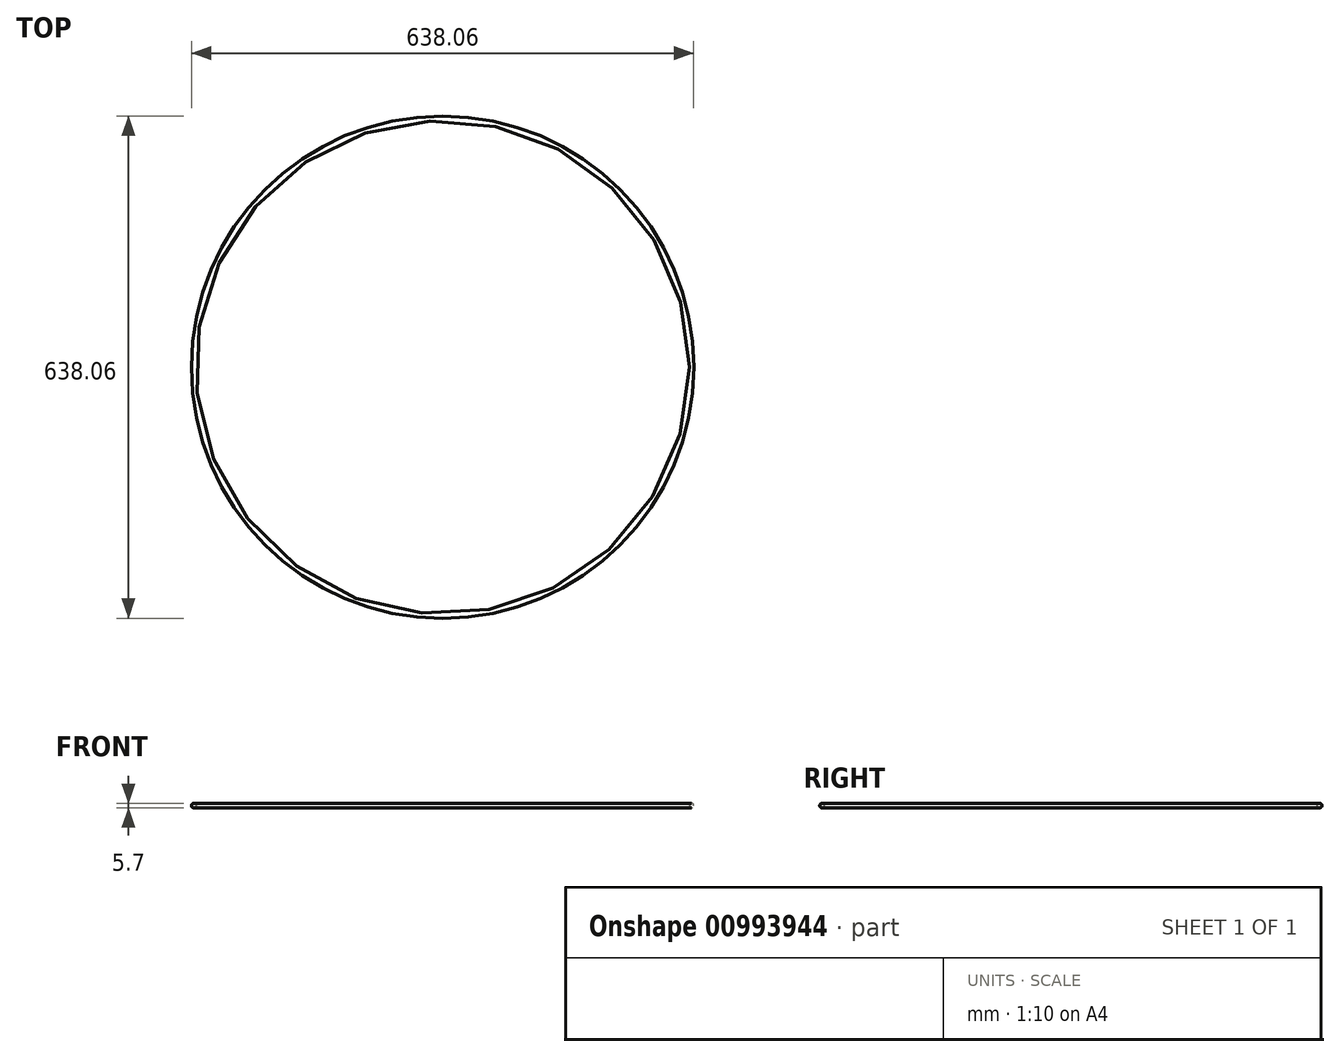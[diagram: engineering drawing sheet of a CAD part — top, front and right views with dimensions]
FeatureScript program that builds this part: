
annotation { "Feature Type Name" : "Feature", "Feature Type Description" : "" }
export const myFeature = defineFeature(function(context is Context, id is Id, definition is map)
    precondition{}
    {
        {
            var Q0;
            Q0=qCreatedBy(makeId("Top.planeOp"),FACE);
            var sketch = newSketch(context, id + "F0", { "sketchPlane" : qUnion([Q0])});
            skCircle(sketch, "E0", {"center": v(0, 0) * mm, "radius": 316.25 * mm});
            skSolve(sketch);
        }
        {
            var Q0;
            Q0=qCreatedBy(makeId("Front.planeOp"),FACE);
            var sketch = newSketch(context, id + "F1", { "sketchPlane" : qUnion([Q0])});
            skCircle(sketch, "E1", {"center": v(-316.18, 0) * mm, "radius": 2.85 * mm});
            skSolve(sketch);
        }
        {
            var Q0;
            Q0=makeQuery(id+"F1.imprint","IMPRINT",FACE,{"disambiguationData":[TD([[makeQuery(id+"F1.imprint","IMPRINT",EDGE,{"derivedFrom":sQuery(id+"F1.wireOp",EDGE,"E1")}),1.0]])]});
            var Q1;
            Q1=sQuery(id+"F0.wireOp",EDGE,"E0");
            sweep(context, id + "F2", {"profiles" : qUnion([Q0]), "path" : qUnion([Q1])});
        }
    });
